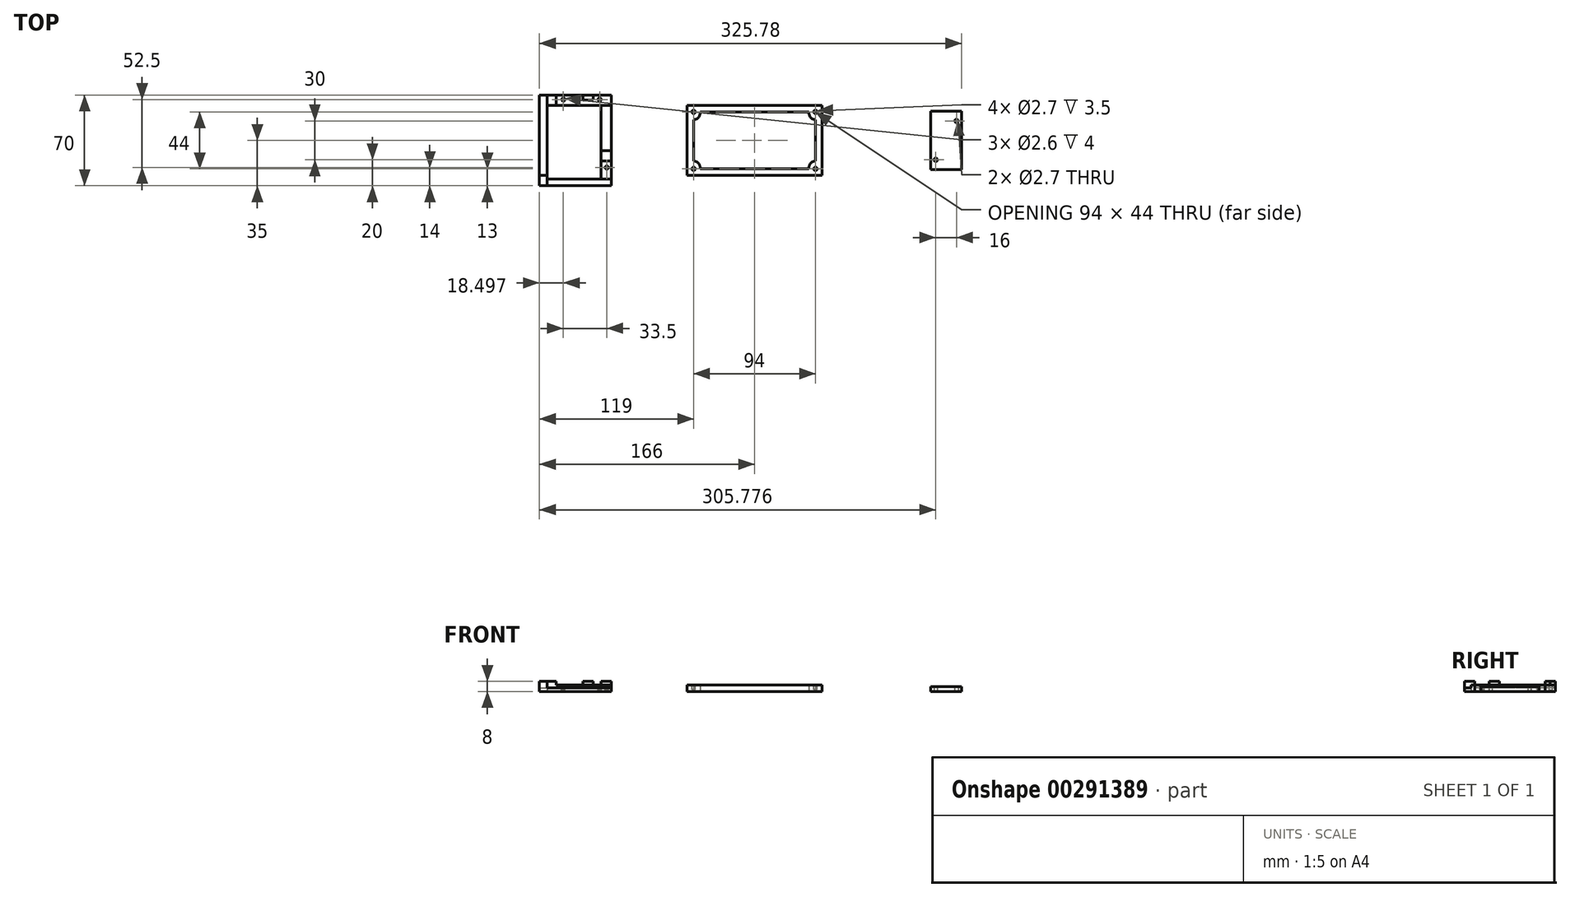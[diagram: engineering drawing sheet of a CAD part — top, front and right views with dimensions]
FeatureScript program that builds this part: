
annotation { "Feature Type Name" : "Feature", "Feature Type Description" : "" }
export const myFeature = defineFeature(function(context is Context, id is Id, definition is map)
    precondition{}
    {
        {
            var Q0;
            Q0=qCreatedBy(makeId("Top.planeOp"),FACE);
            var sketch = newSketch(context, id + "F0", { "sketchPlane" : qUnion([Q0])});
            skLineSegment(sketch, "E0.bottom", {"start": v(52, -27) * mm, "end": v(-52, -27) * mm});
            skLineSegment(sketch, "E0.top", {"start": v(52, 27) * mm, "end": v(-52, 27) * mm});
            skLineSegment(sketch, "E0.left", {"start": v(52, -27) * mm, "end": v(52, 27) * mm});
            skLineSegment(sketch, "E0.right", {"start": v(-52, -27) * mm, "end": v(-52, 27) * mm});
            skPoint(sketch, "E0.middle", {"position": v(0, 0) * mm});
            skLineSegment(sketch, "E1", {"start": v(-42, 22) * mm, "end": v(42, 22) * mm});
            skLineSegment(sketch, "E2", {"start": v(42, 22) * mm, "end": v(42, 16) * mm});
            skLineSegment(sketch, "E3", {"start": v(42, 16) * mm, "end": v(47, 16) * mm});
            skLineSegment(sketch, "E4", {"start": v(47, 16) * mm, "end": v(47, -16) * mm});
            skLineSegment(sketch, "E5", {"start": v(47, -16) * mm, "end": v(42, -16) * mm});
            skLineSegment(sketch, "E6", {"start": v(42, -16) * mm, "end": v(42, -22) * mm});
            skLineSegment(sketch, "E7", {"start": v(42, -22) * mm, "end": v(-42, -22) * mm});
            skLineSegment(sketch, "E8", {"start": v(-42, -22) * mm, "end": v(-42, -16) * mm});
            skLineSegment(sketch, "E9", {"start": v(-42, -16) * mm, "end": v(-47, -16) * mm});
            skLineSegment(sketch, "E10", {"start": v(-47, -16) * mm, "end": v(-47, 16) * mm});
            skLineSegment(sketch, "E11", {"start": v(-47, 16) * mm, "end": v(-42, 16) * mm});
            skLineSegment(sketch, "E12", {"start": v(-42, 16) * mm, "end": v(-42, 22) * mm});
            skSolve(sketch);
        }
        {
            var Q0;
            Q0 = qSketchRegion(id + "F0", true);
            extrude(context, id + "F1", {"entities" : qUnion([Q0]), "depth" : 5 * mm});
        }
        {
            var Q0;
            Q0=makeQuery(id+"F1.opExtrude","CAP_FACE",FACE,{"disambiguationData":[OSD([sQuery(id+"F0.wireOp",EDGE,"E0.bottom"),sQuery(id+"F0.wireOp",EDGE,"E0.top"),sQuery(id+"F0.wireOp",EDGE,"E0.left"),sQuery(id+"F0.wireOp",EDGE,"E0.right"),sQuery(id+"F0.wireOp",EDGE,"E1"),sQuery(id+"F0.wireOp",EDGE,"E2"),sQuery(id+"F0.wireOp",EDGE,"E3"),sQuery(id+"F0.wireOp",EDGE,"E4"),sQuery(id+"F0.wireOp",EDGE,"E5"),sQuery(id+"F0.wireOp",EDGE,"E6"),sQuery(id+"F0.wireOp",EDGE,"E7"),sQuery(id+"F0.wireOp",EDGE,"E8"),sQuery(id+"F0.wireOp",EDGE,"E9"),sQuery(id+"F0.wireOp",EDGE,"E10"),sQuery(id+"F0.wireOp",EDGE,"E11"),sQuery(id+"F0.wireOp",EDGE,"E12")])],"isStart":false});
            var sketch = newSketch(context, id + "F2", { "sketchPlane" : qUnion([Q0])});
            skLineSegment(sketch, "E13.bottom", {"start": v(50, -25) * mm, "end": v(-50, -25) * mm, "construction": true});
            skLineSegment(sketch, "E13.top", {"start": v(50, 25) * mm, "end": v(-50, 25) * mm, "construction": true});
            skLineSegment(sketch, "E13.left", {"start": v(50, -25) * mm, "end": v(50, 25) * mm, "construction": true});
            skLineSegment(sketch, "E13.right", {"start": v(-50, -25) * mm, "end": v(-50, 25) * mm, "construction": true});
            skPoint(sketch, "E13.middle", {"position": v(0, 0) * mm});
            skCircle(sketch, "E14", {"center": v(-47, 22) * mm, "radius": 1.35 * mm});
            skCircle(sketch, "E15", {"center": v(47, 22) * mm, "radius": 1.35 * mm});
            skCircle(sketch, "E16", {"center": v(-47, -22) * mm, "radius": 1.35 * mm});
            skCircle(sketch, "E17", {"center": v(47, -22) * mm, "radius": 1.35 * mm});
            skSolve(sketch);
        }
        {
            var Q0;
            Q0 = qSketchRegion(id + "F2", true);
            extrude(context, id + "F3", {"entities" : qUnion([Q0]), "operationType" : NewBodyOperationType.REMOVE, "oppositeDirection" : true, "depth" : 3.5 * mm});
        }
        {
            var Q0;
            Q0=makeQuery(id+"F1.opExtrude","SWEPT_EDGE",EDGE,{"disambiguationData":[OSD([sQuery(id+"F0.wireOp",EDGE,"E11"),sQuery(id+"F0.wireOp",EDGE,"E12")])]});
            var Q1;
            Q1=makeQuery(id+"F1.opExtrude","SWEPT_EDGE",EDGE,{"disambiguationData":[OSD([sQuery(id+"F0.wireOp",EDGE,"E8"),sQuery(id+"F0.wireOp",EDGE,"E9")])]});
            var Q2;
            Q2=makeQuery(id+"F1.opExtrude","SWEPT_EDGE",EDGE,{"disambiguationData":[OSD([sQuery(id+"F0.wireOp",EDGE,"E2"),sQuery(id+"F0.wireOp",EDGE,"E3")])]});
            var Q3;
            Q3=makeQuery(id+"F1.opExtrude","SWEPT_EDGE",EDGE,{"disambiguationData":[OSD([sQuery(id+"F0.wireOp",EDGE,"E5"),sQuery(id+"F0.wireOp",EDGE,"E6")])]});
            fillet(context, id + "F4", {"entities" : qUnion([Q0, Q1, Q2, Q3]), "radius" : 5 * mm, "tangentPropagation" : true, "allowEdgeOverflow" : false});
        }
        {
            var Q0;
            Q0=qCreatedBy(makeId("Top.planeOp"),FACE);
            var sketch = newSketch(context, id + "F5", { "sketchPlane" : qUnion([Q0])});
            skLineSegment(sketch, "E18.bottom", {"start": v(159.78, -22.5) * mm, "end": v(135.78, -22.5) * mm});
            skLineSegment(sketch, "E18.top", {"start": v(159.78, 22.5) * mm, "end": v(135.78, 22.5) * mm});
            skLineSegment(sketch, "E18.left", {"start": v(159.78, -22.5) * mm, "end": v(159.78, 22.5) * mm});
            skLineSegment(sketch, "E18.right", {"start": v(135.78, -22.5) * mm, "end": v(135.78, 22.5) * mm});
            skPoint(sketch, "E18.middle", {"position": v(147.78, 0) * mm});
            skCircle(sketch, "E19", {"center": v(155.78, 15) * mm, "radius": 1.35 * mm});
            skCircle(sketch, "E20", {"center": v(139.78, -15) * mm, "radius": 1.35 * mm});
            skSolve(sketch);
        }
        {
            var Q0;
            Q0 = qSketchRegion(id + "F5", true);
            extrude(context, id + "F6", {"entities" : qUnion([Q0]), "depth" : 4 * mm});
        }
        {
            var Q0;
            Q0=qCreatedBy(makeId("Top.planeOp"),FACE);
            var sketch = newSketch(context, id + "F7", { "sketchPlane" : qUnion([Q0])});
            skLineSegment(sketch, "E21.bottom", {"start": v(-110.5, -35) * mm, "end": v(-166, -35) * mm});
            skLineSegment(sketch, "E21.top", {"start": v(-110.5, 35) * mm, "end": v(-166, 35) * mm});
            skLineSegment(sketch, "E21.left", {"start": v(-110.5, -35) * mm, "end": v(-110.5, 35) * mm});
            skLineSegment(sketch, "E21.right", {"start": v(-166, -35) * mm, "end": v(-166, 35) * mm});
            skPoint(sketch, "E21.middle", {"position": v(-138.25, 0) * mm});
            skCircle(sketch, "E22", {"center": v(-114, -21) * mm, "radius": 1.35 * mm, "construction": true});
            skCircle(sketch, "E23", {"center": v(-119.5, 31.5) * mm, "radius": 1.35 * mm, "construction": true});
            skCircle(sketch, "E24", {"center": v(-147.5, 31.5) * mm, "radius": 1.35 * mm, "construction": true});
            skLineSegment(sketch, "E25.bottom", {"start": v(-160, 27) * mm, "end": v(-118.5, 27) * mm});
            skLineSegment(sketch, "E25.top", {"start": v(-160, -30) * mm, "end": v(-118.5, -30) * mm});
            skLineSegment(sketch, "E25.left", {"start": v(-160, 27) * mm, "end": v(-160, -30) * mm});
            skLineSegment(sketch, "E25.right", {"start": v(-118.5, 27) * mm, "end": v(-118.5, -30) * mm});
            skSolve(sketch);
        }
        {
            var Q0;
            Q0 = qSketchRegion(id + "F7", true);
            extrude(context, id + "F8", {"entities" : qUnion([Q0]), "depth" : 5 * mm});
        }
        {
            var Q0;
            Q0=makeQuery(id+"F8.opExtrude","CAP_FACE",FACE,{"disambiguationData":[OSD([sQuery(id+"F7.wireOp",EDGE,"E21.bottom"),sQuery(id+"F7.wireOp",EDGE,"E21.top"),sQuery(id+"F7.wireOp",EDGE,"E21.left"),sQuery(id+"F7.wireOp",EDGE,"E21.right"),sQuery(id+"F7.wireOp",EDGE,"E22"),sQuery(id+"F7.wireOp",EDGE,"E23"),sQuery(id+"F7.wireOp",EDGE,"E24")])],"isStart":false});
            var sketch = newSketch(context, id + "F9", { "sketchPlane" : qUnion([Q0])});
            skLineSegment(sketch, "E26.bottom", {"start": v(-160, 35) * mm, "end": v(-153, 35) * mm});
            skLineSegment(sketch, "E26.top", {"start": v(-160, 27) * mm, "end": v(-153, 27) * mm});
            skLineSegment(sketch, "E26.left", {"start": v(-160, 35) * mm, "end": v(-160, 27) * mm});
            skLineSegment(sketch, "E26.right", {"start": v(-153, 35) * mm, "end": v(-153, 27) * mm});
            skLineSegment(sketch, "E27.bottom", {"start": v(-132.5, 35) * mm, "end": v(-124.5, 35) * mm});
            skLineSegment(sketch, "E27.top", {"start": v(-132.5, 31) * mm, "end": v(-124.5, 31) * mm});
            skLineSegment(sketch, "E27.left", {"start": v(-132.5, 35) * mm, "end": v(-132.5, 31) * mm});
            skLineSegment(sketch, "E27.right", {"start": v(-124.5, 35) * mm, "end": v(-124.5, 31) * mm});
            skLineSegment(sketch, "E28.bottom", {"start": v(-118.5, -8) * mm, "end": v(-110.5, -8) * mm});
            skLineSegment(sketch, "E28.top", {"start": v(-118.5, -16) * mm, "end": v(-110.5, -16) * mm});
            skLineSegment(sketch, "E28.left", {"start": v(-118.5, -8) * mm, "end": v(-118.5, -16) * mm});
            skLineSegment(sketch, "E28.right", {"start": v(-110.5, -8) * mm, "end": v(-110.5, -16) * mm});
            skLineSegment(sketch, "E29.bottom", {"start": v(-166, -27) * mm, "end": v(-160, -27) * mm});
            skLineSegment(sketch, "E29.top", {"start": v(-166, -35) * mm, "end": v(-160, -35) * mm});
            skLineSegment(sketch, "E29.left", {"start": v(-166, -27) * mm, "end": v(-166, -35) * mm});
            skLineSegment(sketch, "E29.right", {"start": v(-160, -27) * mm, "end": v(-160, -35) * mm});
            skSolve(sketch);
        }
        {
            var Q0;
            Q0 = qSketchRegion(id + "F9", true);
            extrude(context, id + "F10", {"entities" : qUnion([Q0]), "operationType" : NewBodyOperationType.ADD, "depth" : 3 * mm});
        }
        {
            var Q0;
            Q0=qCreatedBy(makeId("Top.planeOp"),FACE);
            cPlane(context, id + "F11", {"entities" : qUnion([Q0]), "cplaneType" : CPlaneType.OFFSET, "offset" : 5 * mm, "width" : 150 * mm, "height" : 150 * mm});
        }
        {
            var Q0;
            Q0=qCreatedBy(id+"F11.planeOp",FACE);
            var sketch = newSketch(context, id + "F12", { "sketchPlane" : qUnion([Q0])});
            skLineSegment(sketch, "E30.bottom", {"start": v(-166, 35) * mm, "end": v(-160, 35) * mm});
            skLineSegment(sketch, "E30.top", {"start": v(-166, -27) * mm, "end": v(-160, -27) * mm});
            skLineSegment(sketch, "E30.left", {"start": v(-166, 35) * mm, "end": v(-166, -27) * mm});
            skLineSegment(sketch, "E30.right", {"start": v(-160, 35) * mm, "end": v(-160, -27) * mm});
            skLineSegment(sketch, "E31.bottom", {"start": v(-160, -30) * mm, "end": v(-110.5, -30) * mm});
            skLineSegment(sketch, "E31.top", {"start": v(-160, -35) * mm, "end": v(-110.5, -35) * mm});
            skLineSegment(sketch, "E31.left", {"start": v(-160, -30) * mm, "end": v(-160, -35) * mm});
            skLineSegment(sketch, "E31.right", {"start": v(-110.5, -30) * mm, "end": v(-110.5, -35) * mm});
            skLineSegment(sketch, "E32.bottom", {"start": v(-118.5, 27) * mm, "end": v(-110.5, 27) * mm});
            skLineSegment(sketch, "E32.top", {"start": v(-118.5, -8) * mm, "end": v(-110.5, -8) * mm});
            skLineSegment(sketch, "E32.left", {"start": v(-118.5, 27) * mm, "end": v(-118.5, -8) * mm});
            skLineSegment(sketch, "E32.right", {"start": v(-110.5, 27) * mm, "end": v(-110.5, -8) * mm});
            skSolve(sketch);
        }
        {
            var Q0;
            Q0 = qSketchRegion(id + "F12", true);
            extrude(context, id + "F13", {"entities" : qUnion([Q0]), "operationType" : NewBodyOperationType.REMOVE, "oppositeDirection" : true, "depth" : 2 * mm});
        }
        {
            var Q0;
            {var subQ0=sQuery(id+"F7.wireOp",EDGE,"E21.left");var subQ1=sQuery(id+"F7.wireOp",EDGE,"E21.top");var subQ2=sQuery(id+"F7.wireOp",EDGE,"E25.right");var subQ3=sQuery(id+"F7.wireOp",EDGE,"E25.bottom");Q0=makeQuery(id+"F10.boolean.opBoolean","SPLIT",FACE,{"disambiguationData":[TD([makeQuery(id+"F10.opExtrude","SWEPT_FACE",FACE,{"disambiguationData":[OSD([sQuery(id+"F9.wireOp",EDGE,"E26.right")])]})])],"derivedFrom":makeQuery(id+"F8.opExtrude","CAP_FACE",FACE,{"disambiguationData":[OSD([sQuery(id+"F7.wireOp",EDGE,"E21.bottom"),subQ1,subQ0,sQuery(id+"F7.wireOp",EDGE,"E21.right"),subQ3,sQuery(id+"F7.wireOp",EDGE,"E25.top"),sQuery(id+"F7.wireOp",EDGE,"E25.left"),subQ2])],"isStart":false})});}
            var sketch = newSketch(context, id + "F14", { "sketchPlane" : qUnion([Q0])});
            skCircle(sketch, "E33", {"center": v(-147.5, 31.5) * mm, "radius": 1.3 * mm});
            skCircle(sketch, "E34", {"center": v(-119.5, 31.5) * mm, "radius": 1.3 * mm});
            skCircle(sketch, "E35", {"center": v(-114, -21) * mm, "radius": 1.3 * mm});
            skSolve(sketch);
        }
        {
            var Q0;
            Q0 = qSketchRegion(id + "F14", true);
            extrude(context, id + "F15", {"entities" : qUnion([Q0]), "operationType" : NewBodyOperationType.REMOVE, "oppositeDirection" : true, "depth" : 4 * mm});
        }
    });
